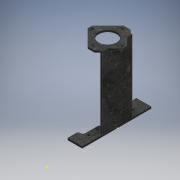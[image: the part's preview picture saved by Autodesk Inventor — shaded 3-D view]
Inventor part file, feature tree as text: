
AUTODESK INVENTOR PART (.ipt)
format: ipt  version: 2018 (Build 220112000, 112)  size: 326,656 bytes
history: native  units: mm
features: sketch x12, reference x12, extrude x9, other x4, plane x2, fillet x1, chamfer x1
ambient origin geometry x8: Origin, YZ Plane, XZ Plane, XY Plane, X Axis, Y Axis, Z Axis, Center Point
bodies: Solid1 (feature_tree)
feature tree (41):
  extrude  "Extrusion1"  Depth=13.0mm
  fillet  "Fillet1"  Radius=30.0mm
  extrude  "Extrusion2"  Depth=55.0mm
  extrude  "Extrusion3"  Depth=16.0mm
  extrude  "Extrusion4"  Depth=7.0mm
  extrude  "Extrusion5"  Depth=6.0mm
  chamfer  "Chamfer1"  Distance=241.0mm
  extrude  "Extrusion6"  Depth=85.0mm TaperAngle=0.0deg
  plane  "Work Plane1"
  plane  "Work Plane2"
  sketch  "Sketch8"  dims[d17=10.0mm d18=10.0mm]
  sketch  "Sketch11"  dims[d19=4.0mm d20=4.0mm]
  sketch  "Sketch13"  dims[d23=7.0mm d24=0.0mm d25=6.0mm]
  sketch  "Sketch15"  dims[d26=40.0mm]
  extrude  "Extrusion19"  Depth=10.0mm
  extrude  "Extrusion20"  Depth=4.0mm
  extrude  "Extrusion21"  Depth=6.0mm
  sketch  "Sketch1"  dims[d0=230.0mm d1=13.0mm d2=30.0mm]
  reference  "Reference1"
  sketch  "Sketch2"  dims[d3=55.0mm d4=55.0mm]
  reference  "Reference2"
  reference  "Reference3"
  sketch  "Sketch3"  dims[d5=55.0mm d6=16.0mm]
  sketch  "Sketch4"  dims[d7=6.0mm d8=0.0mm d9=7.0mm]
  reference  "Reference4"
  reference  "Reference5"
  reference  "Reference6"
  reference  "Reference7"
  sketch  "Sketch5"  dims[d10=100.0mm d11=6.0mm d12=241.0mm d13=0.0mm]
  sketch  "Sketch6"  dims[d14=6.0mm d15=85.0mm d16=0.0mm]
  reference  "Reference8"
  reference  "Reference9"
  reference  "Reference10"
  reference  "Reference11"
  reference  "Reference12"
  sketch  "Sketch23"  dims[d27=26.0mm d28=0.0mm]
  sketch  "Sketch24"  dims[d29=13.0mm d30=2.0mm d31=45.0deg d33=0.5mm d34=7.0mm d35=0.0mm d38=-10.0mm d56=42.0mm d57=24.5mm d58=7.0mm d59=74.0mm d60=21.5mm d61=8.0mm d62=42.0mm d63=74.0mm d64=7.0mm d65=8.0mm d85=16.0mm d86=0.0mm d87=9.0mm d88=24.0mm d89=102.38mm d90=9.0mm d91=102.38mm d92=24.0mm d93=10.0mm d94=0.0mm d95=8.0mm d96=8.0mm d97=20.0mm d98=20.0mm d99=135.0mm d100=10.0mm d101=0.0mm]
  other  "Lathe Model 2018.iam"
  other  "saddle:1"
  other  "Servo Motor:2"
  other  "Body:1"
